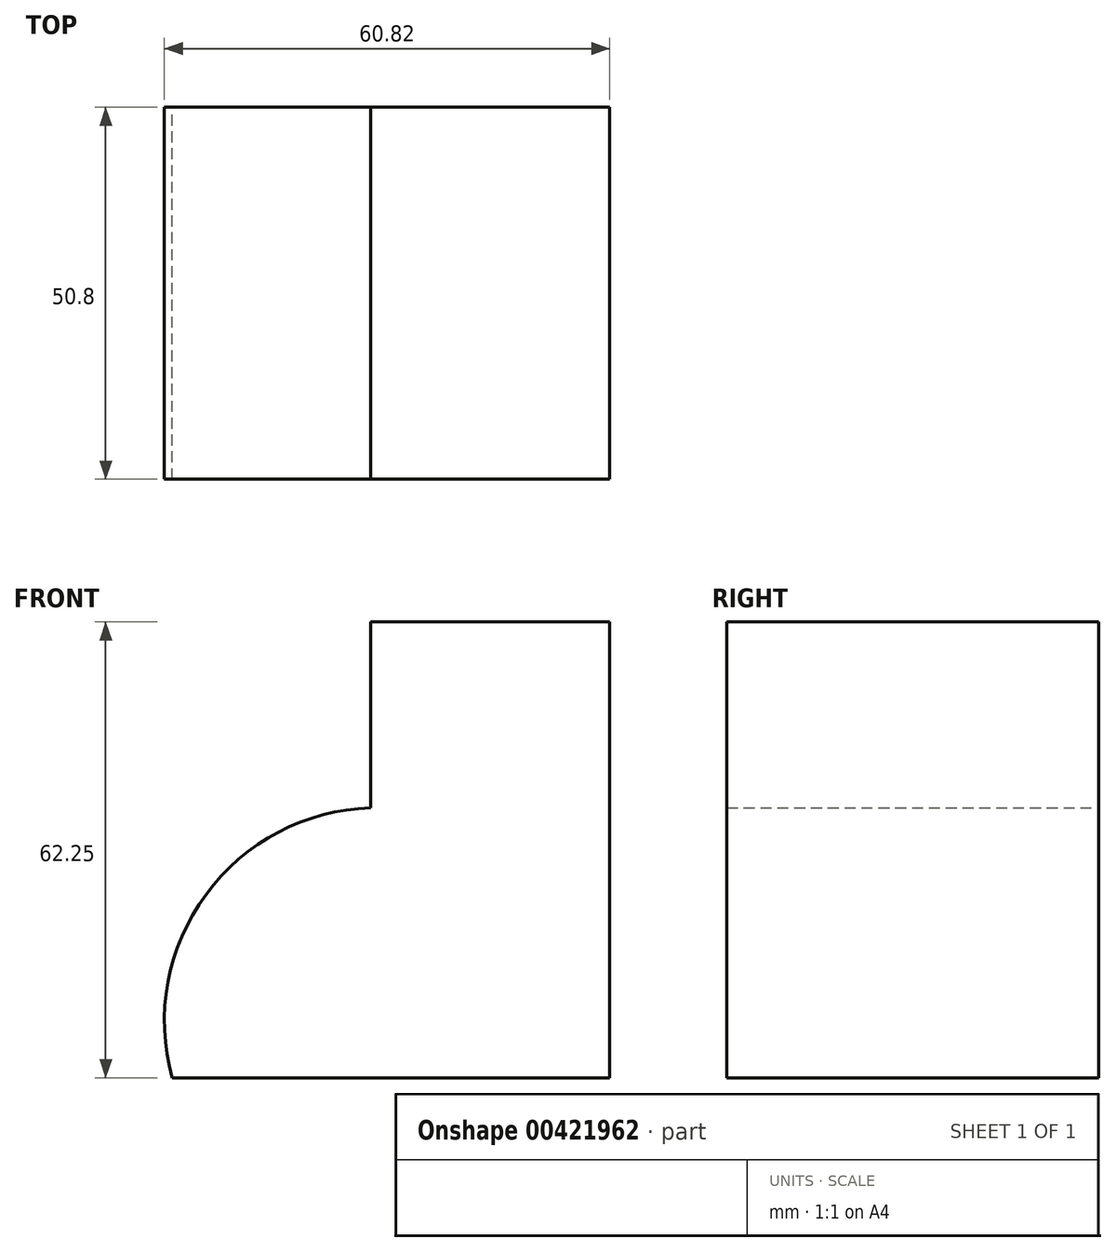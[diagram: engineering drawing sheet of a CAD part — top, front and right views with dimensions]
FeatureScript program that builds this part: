
annotation { "Feature Type Name" : "Feature", "Feature Type Description" : "" }
export const myFeature = defineFeature(function(context is Context, id is Id, definition is map)
    precondition{}
    {
        {
            var Q0;
            Q0=qCreatedBy(makeId("Front.planeOp"),FACE);
            var sketch = newSketch(context, id + "F0", { "sketchPlane" : qUnion([Q0])});
            skLineSegment(sketch, "E0", {"start": v(-32.65, 36.85) * mm, "end": v(-32.65, 62.25) * mm});
            skLineSegment(sketch, "E1", {"start": v(-32.65, 62.25) * mm, "end": v(0, 62.25) * mm});
            skLineSegment(sketch, "E2", {"start": v(0, 62.25) * mm, "end": v(0, 0) * mm});
            skLineSegment(sketch, "E3", {"start": v(0, 0) * mm, "end": v(-59.77, 0) * mm});
            skArc(sketch, "E4", {"start": v(-32.65, 36.85) * mm, "mid": v(-55.16, 25) * mm, "end": v(-59.77, 0) * mm});
            skSolve(sketch);
        }
        {
            var Q0;
            Q0=makeQuery(id+"F0.imprint","IMPRINT",FACE,{"disambiguationData":[TD([[makeQuery(id+"F0.imprint","IMPRINT",EDGE,{"derivedFrom":sQuery(id+"F0.wireOp",EDGE,"E0")}),-1.0]])]});
            extrude(context, id + "F1", {"entities" : qUnion([Q0]), "depth" : 50.8 * mm});
        }
    });
